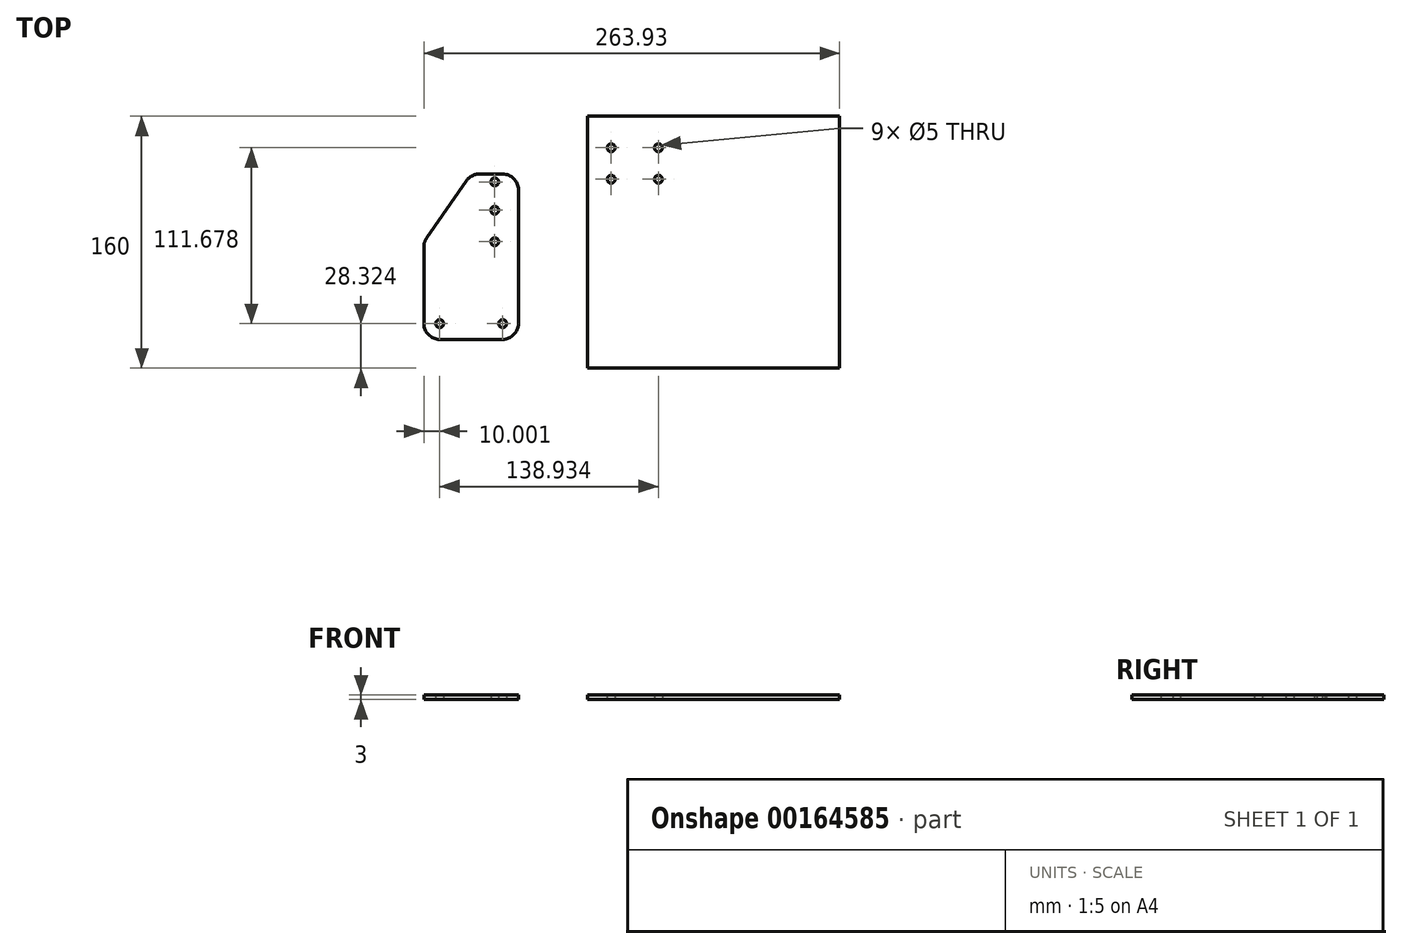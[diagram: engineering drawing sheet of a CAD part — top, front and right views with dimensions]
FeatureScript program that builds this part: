
annotation { "Feature Type Name" : "Feature", "Feature Type Description" : "" }
export const myFeature = defineFeature(function(context is Context, id is Id, definition is map)
    precondition{}
    {
        {
            var Q0;
            Q0=qCreatedBy(makeId("Top.planeOp"),FACE);
            var sketch = newSketch(context, id + "F0", { "sketchPlane" : qUnion([Q0])});
            skLineSegment(sketch, "E0.bottom", {"start": v(-3.43, 48.53) * mm, "end": v(26.57, 48.53) * mm});
            skLineSegment(sketch, "E0.top", {"start": v(-33.43, -56.47) * mm, "end": v(26.57, -56.47) * mm});
            skLineSegment(sketch, "E0.left", {"start": v(-33.43, 5.46) * mm, "end": v(-33.43, -56.47) * mm});
            skLineSegment(sketch, "E0.right", {"start": v(26.57, 48.53) * mm, "end": v(26.57, -56.47) * mm});
            skCircle(sketch, "E1", {"center": v(11.57, 43.53) * mm, "radius": 2.5 * mm});
            skCircle(sketch, "E2", {"center": v(11.57, 25.53) * mm, "radius": 2.5 * mm});
            skCircle(sketch, "E3", {"center": v(11.57, 5.53) * mm, "radius": 2.5 * mm});
            skCircle(sketch, "E4", {"center": v(16.57, -46.47) * mm, "radius": 2.5 * mm});
            skCircle(sketch, "E5", {"center": v(-23.43, -46.47) * mm, "radius": 2.5 * mm});
            skLineSegment(sketch, "E6", {"start": v(-3.43, 48.53) * mm, "end": v(-33.43, 5.46) * mm});
            skPoint(sketch, "E7.orphan", {"position": v(-33.43, 48.53) * mm});
            skSolve(sketch);
        }
        {
            var Q0;
            Q0 = qSketchRegion(id + "F0", true);
            extrude(context, id + "F1", {"entities" : qUnion([Q0]), "depth" : 3 * mm});
        }
        {
            var Q0;
            Q0=makeQuery(id+"F1.opExtrude","SWEPT_EDGE",EDGE,{"disambiguationData":[OSD([sQuery(id+"F0.wireOp",EDGE,"E0.bottom"),sQuery(id+"F0.wireOp",EDGE,"E0.right")])]});
            var Q1;
            Q1=makeQuery(id+"F1.opExtrude","SWEPT_EDGE",EDGE,{"disambiguationData":[OSD([sQuery(id+"F0.wireOp",EDGE,"E0.bottom"),sQuery(id+"F0.wireOp",EDGE,"E6")])]});
            var Q2;
            Q2=makeQuery(id+"F1.opExtrude","SWEPT_EDGE",EDGE,{"disambiguationData":[OSD([sQuery(id+"F0.wireOp",EDGE,"E0.top"),sQuery(id+"F0.wireOp",EDGE,"E0.right")])]});
            var Q3;
            Q3=makeQuery(id+"F1.opExtrude","SWEPT_EDGE",EDGE,{"disambiguationData":[OSD([sQuery(id+"F0.wireOp",EDGE,"E0.top"),sQuery(id+"F0.wireOp",EDGE,"E0.left")])]});
            var Q4;
            Q4=makeQuery(id+"F1.opExtrude","SWEPT_EDGE",EDGE,{"disambiguationData":[OSD([sQuery(id+"F0.wireOp",EDGE,"E0.left"),sQuery(id+"F0.wireOp",EDGE,"E6")])]});
            fillet(context, id + "F2", {"entities" : qUnion([Q0, Q1, Q2, Q3, Q4]), "radius" : 10 * mm, "tangentPropagation" : true, "allowEdgeOverflow" : false});
        }
        {
            var Q0;
            Q0=qCreatedBy(makeId("Top.planeOp"),FACE);
            var sketch = newSketch(context, id + "F3", { "sketchPlane" : qUnion([Q0])});
            skLineSegment(sketch, "E8.bottom", {"start": v(70.5, 85.21) * mm, "end": v(230.5, 85.21) * mm});
            skLineSegment(sketch, "E8.top", {"start": v(70.5, -74.79) * mm, "end": v(230.5, -74.79) * mm});
            skLineSegment(sketch, "E8.left", {"start": v(70.5, 85.21) * mm, "end": v(70.5, -74.79) * mm});
            skLineSegment(sketch, "E8.right", {"start": v(230.5, 85.21) * mm, "end": v(230.5, -74.79) * mm});
            skCircle(sketch, "E9", {"center": v(85.5, 65.21) * mm, "radius": 2.5 * mm});
            skCircle(sketch, "E10", {"center": v(85.5, 45.21) * mm, "radius": 2.5 * mm});
            skCircle(sketch, "E11", {"center": v(115.5, 65.21) * mm, "radius": 2.5 * mm});
            skCircle(sketch, "E12", {"center": v(115.5, 45.21) * mm, "radius": 2.5 * mm});
            skSolve(sketch);
        }
        {
            var Q0;
            Q0 = qSketchRegion(id + "F3", true);
            extrude(context, id + "F4", {"entities" : qUnion([Q0]), "depth" : 3 * mm, "offsetDistance" : 25 * mm});
        }
    });
